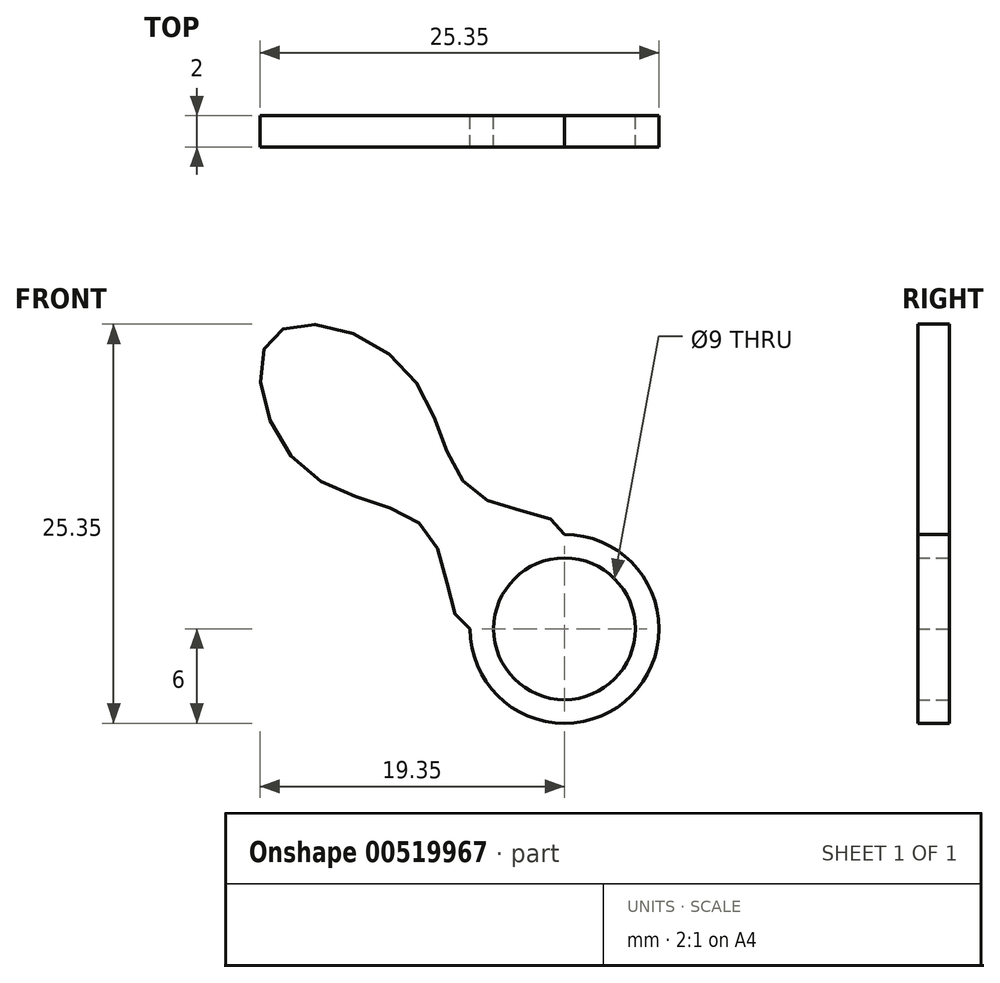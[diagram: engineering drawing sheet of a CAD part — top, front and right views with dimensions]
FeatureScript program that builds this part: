
annotation { "Feature Type Name" : "Feature", "Feature Type Description" : "" }
export const myFeature = defineFeature(function(context is Context, id is Id, definition is map)
    precondition{}
    {
        {
            var Q0;
            Q0=qCreatedBy(makeId("Front.planeOp"),FACE);
            var sketch = newSketch(context, id + "F0", { "sketchPlane" : qUnion([Q0])});
            skCircle(sketch, "E0", {"center": v(0, 0) * mm, "radius": 4.5 * mm});
            skCircle(sketch, "E1", {"center": v(0, 0) * mm, "radius": 6 * mm});
            skFitSpline(sketch, "E2", {"points": [v(-6, 0) * mm, v(-8.48, 5.91) * mm, v(-16.52, 10.1) * mm, v(-18.58, 18.58) * mm, v(-10.1, 16.52) * mm, v(-5.47, 8.47) * mm, v(0, 6) * mm, v(-6, 0) * mm]});
            skSolve(sketch);
        }
        {
            var Q0;
            Q0 = qSketchRegion(id + "F0", true);
            extrude(context, id + "F1", {"entities" : qUnion([Q0]), "depth" : 2 * mm, "offsetDistance" : 25 * mm});
        }
    });
